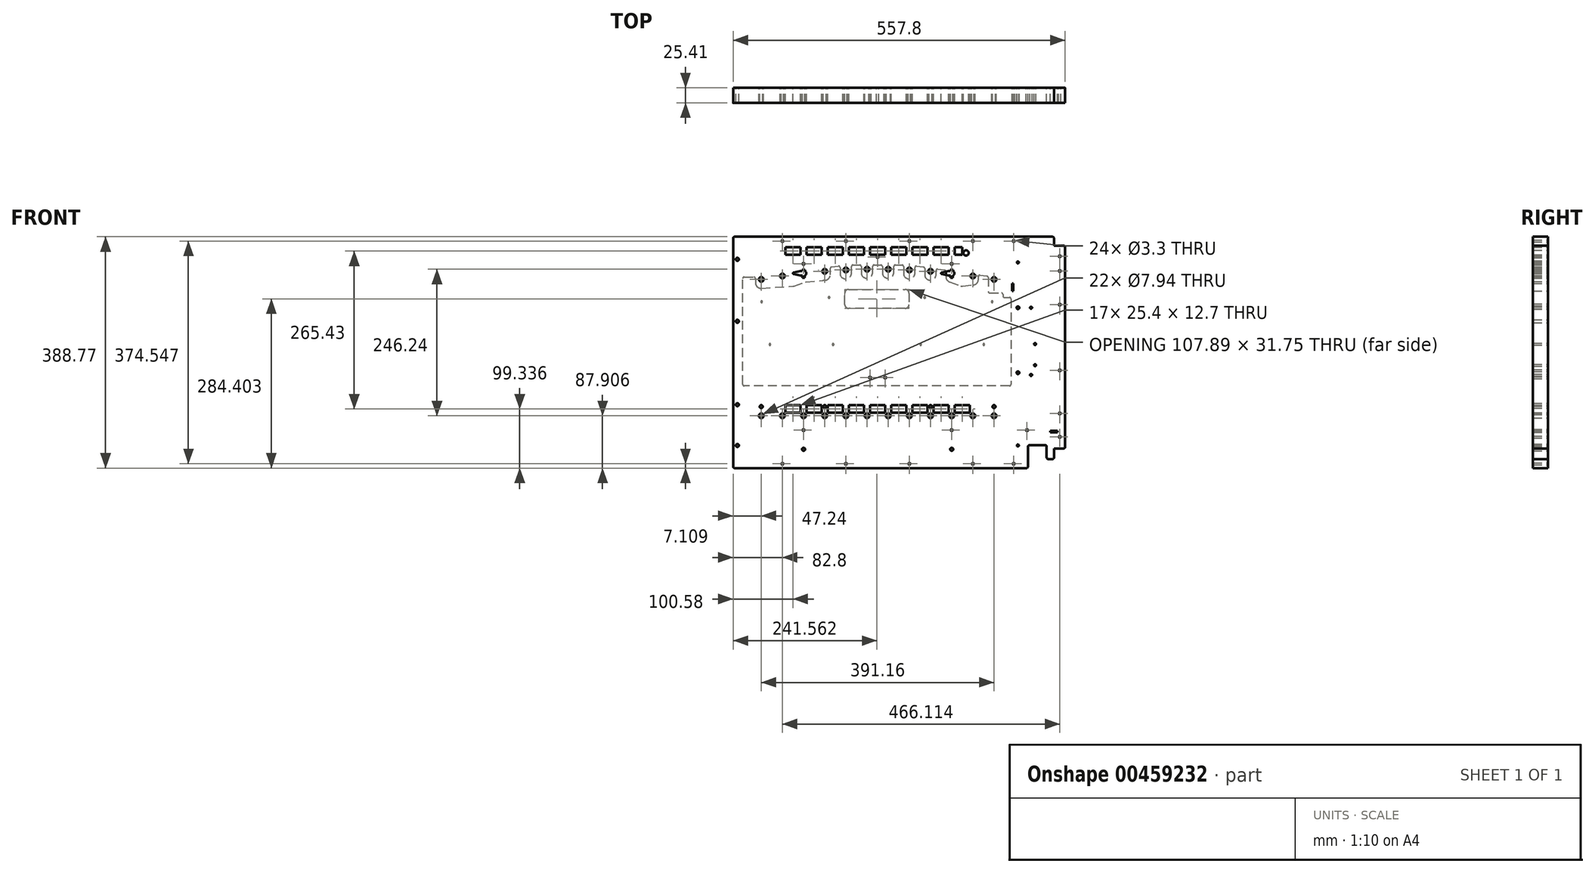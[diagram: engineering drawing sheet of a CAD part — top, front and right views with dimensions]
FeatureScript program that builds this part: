
annotation { "Feature Type Name" : "Feature", "Feature Type Description" : "" }
export const myFeature = defineFeature(function(context is Context, id is Id, definition is map)
    precondition{}
    {
        {
            var Q0;
            Q0=qCreatedBy(makeId("Front.planeOp"),FACE);
            var sketch = newSketch(context, id + "F0", { "sketchPlane" : qUnion([Q0])});
            skCircle(sketch, "E0", {"center": v(270.01, 168.97) * mm, "radius": 1.65 * mm});
            skCircle(sketch, "E1", {"center": v(270.01, 144.35) * mm, "radius": 1.65 * mm});
            skCircle(sketch, "E2", {"center": v(270.01, 87.69) * mm, "radius": 1.65 * mm});
            skCircle(sketch, "E3", {"center": v(270.01, -22.8) * mm, "radius": 1.65 * mm});
            skCircle(sketch, "E4", {"center": v(270.01, -134.56) * mm, "radius": 1.65 * mm});
            skCircle(sketch, "E5", {"center": v(270.01, -95.2) * mm, "radius": 1.65 * mm});
            skCircle(sketch, "E6", {"center": v(-196.1, -179.8) * mm, "radius": 1.65 * mm});
            skCircle(sketch, "E7", {"center": v(-89.42, -179.8) * mm, "radius": 1.65 * mm});
            skCircle(sketch, "E8", {"center": v(17.26, -179.8) * mm, "radius": 1.65 * mm});
            skCircle(sketch, "E9", {"center": v(123.94, -179.8) * mm, "radius": 1.65 * mm});
            skCircle(sketch, "E10", {"center": v(192.52, -179.8) * mm, "radius": 1.65 * mm});
            skCircle(sketch, "E11", {"center": v(-196.1, 194.75) * mm, "radius": 1.65 * mm});
            skCircle(sketch, "E12", {"center": v(-89.42, 194.75) * mm, "radius": 1.65 * mm});
            skCircle(sketch, "E13", {"center": v(17.26, 194.75) * mm, "radius": 1.65 * mm});
            skCircle(sketch, "E14", {"center": v(123.94, 194.75) * mm, "radius": 1.65 * mm});
            skCircle(sketch, "E15", {"center": v(192.52, 194.75) * mm, "radius": 1.65 * mm});
            skCircle(sketch, "E16", {"center": v(-196.1, 136) * mm, "radius": 3.97 * mm});
            skCircle(sketch, "E17", {"center": v(-124.98, 143.87) * mm, "radius": 3.97 * mm});
            skCircle(sketch, "E18", {"center": v(-89.42, 146.12) * mm, "radius": 3.97 * mm});
            skCircle(sketch, "E19", {"center": v(-53.86, 147.24) * mm, "radius": 3.97 * mm});
            skCircle(sketch, "E20", {"center": v(17.26, 146.12) * mm, "radius": 3.97 * mm});
            skCircle(sketch, "E21", {"center": v(-18.3, 147.24) * mm, "radius": 3.97 * mm});
            skCircle(sketch, "E22", {"center": v(52.82, 143.87) * mm, "radius": 3.97 * mm});
            skCircle(sketch, "E23", {"center": v(123.94, 136) * mm, "radius": 3.97 * mm});
            skCircle(sketch, "E24", {"center": v(-196.1, -99) * mm, "radius": 3.97 * mm});
            skCircle(sketch, "E25", {"center": v(-160.54, -99) * mm, "radius": 3.97 * mm});
            skCircle(sketch, "E26", {"center": v(-124.98, -99) * mm, "radius": 3.97 * mm});
            skCircle(sketch, "E27", {"center": v(-89.42, -99) * mm, "radius": 3.97 * mm});
            skCircle(sketch, "E28", {"center": v(-53.86, -99) * mm, "radius": 3.97 * mm});
            skCircle(sketch, "E29", {"center": v(-18.3, -99) * mm, "radius": 3.97 * mm});
            skCircle(sketch, "E30", {"center": v(17.26, -99) * mm, "radius": 3.97 * mm});
            skCircle(sketch, "E31", {"center": v(52.82, -99) * mm, "radius": 3.97 * mm});
            skCircle(sketch, "E32", {"center": v(88.38, -99) * mm, "radius": 3.97 * mm});
            skCircle(sketch, "E33", {"center": v(123.94, -99) * mm, "radius": 3.97 * mm});
            skCircle(sketch, "E34", {"center": v(159.5, 130.33) * mm, "radius": 3.97 * mm});
            skCircle(sketch, "E35", {"center": v(159.5, -99) * mm, "radius": 3.97 * mm});
            skCircle(sketch, "E36", {"center": v(-231.66, -99) * mm, "radius": 3.97 * mm});
            skCircle(sketch, "E37", {"center": v(-231.66, 130.33) * mm, "radius": 3.97 * mm});
            skCircle(sketch, "E38", {"center": v(-271.8, 163.89) * mm, "radius": 2.54 * mm});
            skCircle(sketch, "E39", {"center": v(-271.8, 59.75) * mm, "radius": 2.54 * mm});
            skCircle(sketch, "E40", {"center": v(-271.8, -148.94) * mm, "radius": 2.54 * mm});
            skCircle(sketch, "E41", {"center": v(-160.54, 156.27) * mm, "radius": 1.65 * mm});
            skCircle(sketch, "E42", {"center": v(88.38, 156.27) * mm, "radius": 1.65 * mm});
            skCircle(sketch, "E43", {"center": v(-36.08, 167.95) * mm, "radius": 1.65 * mm});
            skCircle(sketch, "E44", {"center": v(199.63, 82.6) * mm, "radius": 2.29 * mm});
            skCircle(sketch, "E45", {"center": v(221.73, 82.6) * mm, "radius": 1.66 * mm});
            skCircle(sketch, "E46", {"center": v(199.63, -26.61) * mm, "radius": 2.29 * mm});
            skCircle(sketch, "E47", {"center": v(221.73, -30.42) * mm, "radius": 1.66 * mm});
            skCircle(sketch, "E48", {"center": v(-160.54, -155.3) * mm, "radius": 2.54 * mm});
            skCircle(sketch, "E49", {"center": v(88.38, -155.3) * mm, "radius": 2.54 * mm});
            skCircle(sketch, "E50", {"center": v(-231.66, -83.76) * mm, "radius": 2.54 * mm});
            skCircle(sketch, "E51", {"center": v(159.5, -83.76) * mm, "radius": 2.54 * mm});
            skCircle(sketch, "E52", {"center": v(-160.54, -123.13) * mm, "radius": 1.65 * mm});
            skCircle(sketch, "E53", {"center": v(88.38, -123.13) * mm, "radius": 1.65 * mm});
            skCircle(sketch, "E54", {"center": v(-271.8, -80.36) * mm, "radius": 2.54 * mm});
            skCircle(sketch, "E55", {"center": v(-124.98, -83.76) * mm, "radius": 2.54 * mm});
            skCircle(sketch, "E56", {"center": v(52.82, -83.76) * mm, "radius": 2.54 * mm});
            skCircle(sketch, "E57", {"center": v(228.49, -13.91) * mm, "radius": 1.66 * mm});
            skCircle(sketch, "E58", {"center": v(228.49, 21.65) * mm, "radius": 1.66 * mm});
            skCircle(sketch, "E59", {"center": v(112.5, 174.6) * mm, "radius": 4.45 * mm});
            skCircle(sketch, "E60", {"center": v(199.63, 158.8) * mm, "radius": 1.66 * mm});
            skCircle(sketch, "E61", {"center": v(199.63, -148.94) * mm, "radius": 1.66 * mm});
            skCircle(sketch, "E62", {"center": v(-48.78, -34.87) * mm, "radius": 1.65 * mm});
            skCircle(sketch, "E63", {"center": v(-23.38, -34.87) * mm, "radius": 1.65 * mm});
            skCircle(sketch, "E64", {"center": v(214.97, -123.13) * mm, "radius": 1.65 * mm});
            skLineSegment(sketch, "E65", {"start": v(-48.78, 171.5) * mm, "end": v(-23.38, 171.5) * mm});
            skLineSegment(sketch, "E66", {"start": v(-23.38, 171.5) * mm, "end": v(-23.38, 184.2) * mm});
            skLineSegment(sketch, "E67", {"start": v(-23.38, 184.2) * mm, "end": v(-48.78, 184.2) * mm});
            skLineSegment(sketch, "E68", {"start": v(-48.78, 184.2) * mm, "end": v(-48.78, 171.5) * mm});
            skLineSegment(sketch, "E69", {"start": v(-58.94, 184.2) * mm, "end": v(-84.34, 184.2) * mm});
            skLineSegment(sketch, "E70", {"start": v(-84.34, 184.2) * mm, "end": v(-84.34, 171.5) * mm});
            skLineSegment(sketch, "E71", {"start": v(-84.34, 171.5) * mm, "end": v(-58.94, 171.5) * mm});
            skLineSegment(sketch, "E72", {"start": v(-58.94, 171.5) * mm, "end": v(-58.94, 184.2) * mm});
            skLineSegment(sketch, "E73", {"start": v(-94.5, 184.2) * mm, "end": v(-119.9, 184.2) * mm});
            skLineSegment(sketch, "E74", {"start": v(-119.9, 184.2) * mm, "end": v(-119.9, 171.5) * mm});
            skLineSegment(sketch, "E75", {"start": v(-119.9, 171.5) * mm, "end": v(-94.5, 171.5) * mm});
            skLineSegment(sketch, "E76", {"start": v(-94.5, 171.5) * mm, "end": v(-94.5, 184.2) * mm});
            skLineSegment(sketch, "E77", {"start": v(-130.06, 184.2) * mm, "end": v(-155.46, 184.2) * mm});
            skLineSegment(sketch, "E78", {"start": v(-155.46, 184.2) * mm, "end": v(-155.46, 171.5) * mm});
            skLineSegment(sketch, "E79", {"start": v(-155.46, 171.5) * mm, "end": v(-130.06, 171.5) * mm});
            skLineSegment(sketch, "E80", {"start": v(-130.06, 171.5) * mm, "end": v(-130.06, 184.2) * mm});
            skLineSegment(sketch, "E81", {"start": v(-165.62, 184.2) * mm, "end": v(-191.02, 184.2) * mm});
            skLineSegment(sketch, "E82", {"start": v(-191.02, 184.2) * mm, "end": v(-191.02, 171.5) * mm});
            skLineSegment(sketch, "E83", {"start": v(-191.02, 171.5) * mm, "end": v(-165.62, 171.5) * mm});
            skLineSegment(sketch, "E84", {"start": v(-165.62, 171.5) * mm, "end": v(-165.62, 184.2) * mm});
            skLineSegment(sketch, "E85", {"start": v(-13.22, 171.5) * mm, "end": v(12.18, 171.5) * mm});
            skLineSegment(sketch, "E86", {"start": v(12.18, 171.5) * mm, "end": v(12.18, 184.2) * mm});
            skLineSegment(sketch, "E87", {"start": v(12.18, 184.2) * mm, "end": v(-13.22, 184.2) * mm});
            skLineSegment(sketch, "E88", {"start": v(-13.22, 184.2) * mm, "end": v(-13.22, 171.5) * mm});
            skLineSegment(sketch, "E89", {"start": v(22.34, 171.5) * mm, "end": v(47.74, 171.5) * mm});
            skLineSegment(sketch, "E90", {"start": v(47.74, 171.5) * mm, "end": v(47.74, 184.2) * mm});
            skLineSegment(sketch, "E91", {"start": v(47.74, 184.2) * mm, "end": v(22.34, 184.2) * mm});
            skLineSegment(sketch, "E92", {"start": v(22.34, 184.2) * mm, "end": v(22.34, 171.5) * mm});
            skLineSegment(sketch, "E93", {"start": v(57.9, 171.5) * mm, "end": v(83.3, 171.5) * mm});
            skLineSegment(sketch, "E94", {"start": v(83.3, 171.5) * mm, "end": v(83.3, 184.2) * mm});
            skLineSegment(sketch, "E95", {"start": v(83.3, 184.2) * mm, "end": v(57.9, 184.2) * mm});
            skLineSegment(sketch, "E96", {"start": v(57.9, 184.2) * mm, "end": v(57.9, 171.5) * mm});
            skLineSegment(sketch, "E97", {"start": v(93.46, 171.5) * mm, "end": v(106.16, 171.5) * mm});
            skLineSegment(sketch, "E98", {"start": v(106.16, 171.5) * mm, "end": v(106.16, 184.2) * mm});
            skLineSegment(sketch, "E99", {"start": v(106.16, 184.2) * mm, "end": v(93.46, 184.2) * mm});
            skLineSegment(sketch, "E100", {"start": v(93.46, 184.2) * mm, "end": v(93.46, 171.5) * mm});
            skLineSegment(sketch, "E101", {"start": v(-48.78, -93.92) * mm, "end": v(-23.38, -93.92) * mm});
            skLineSegment(sketch, "E102", {"start": v(-23.38, -93.92) * mm, "end": v(-23.38, -81.22) * mm});
            skLineSegment(sketch, "E103", {"start": v(-23.38, -81.22) * mm, "end": v(-48.78, -81.22) * mm});
            skLineSegment(sketch, "E104", {"start": v(-48.78, -81.22) * mm, "end": v(-48.78, -93.92) * mm});
            skLineSegment(sketch, "E105", {"start": v(-58.94, -81.22) * mm, "end": v(-84.34, -81.22) * mm});
            skLineSegment(sketch, "E106", {"start": v(-84.34, -81.22) * mm, "end": v(-84.34, -93.92) * mm});
            skLineSegment(sketch, "E107", {"start": v(-84.34, -93.92) * mm, "end": v(-58.94, -93.92) * mm});
            skLineSegment(sketch, "E108", {"start": v(-58.94, -93.92) * mm, "end": v(-58.94, -81.22) * mm});
            skLineSegment(sketch, "E109", {"start": v(-94.5, -81.22) * mm, "end": v(-119.9, -81.22) * mm});
            skLineSegment(sketch, "E110", {"start": v(-119.9, -81.22) * mm, "end": v(-119.9, -93.92) * mm});
            skLineSegment(sketch, "E111", {"start": v(-119.9, -93.92) * mm, "end": v(-94.5, -93.92) * mm});
            skLineSegment(sketch, "E112", {"start": v(-94.5, -93.92) * mm, "end": v(-94.5, -81.22) * mm});
            skLineSegment(sketch, "E113", {"start": v(-130.06, -81.22) * mm, "end": v(-155.46, -81.22) * mm});
            skLineSegment(sketch, "E114", {"start": v(-155.46, -81.22) * mm, "end": v(-155.46, -93.92) * mm});
            skLineSegment(sketch, "E115", {"start": v(-155.46, -93.92) * mm, "end": v(-130.06, -93.92) * mm});
            skLineSegment(sketch, "E116", {"start": v(-130.06, -93.92) * mm, "end": v(-130.06, -81.22) * mm});
            skLineSegment(sketch, "E117", {"start": v(-165.62, -81.22) * mm, "end": v(-191.02, -81.22) * mm});
            skLineSegment(sketch, "E118", {"start": v(-191.02, -81.22) * mm, "end": v(-191.02, -93.92) * mm});
            skLineSegment(sketch, "E119", {"start": v(-191.02, -93.92) * mm, "end": v(-165.62, -93.92) * mm});
            skLineSegment(sketch, "E120", {"start": v(-165.62, -93.92) * mm, "end": v(-165.62, -81.22) * mm});
            skLineSegment(sketch, "E121", {"start": v(-13.22, -93.92) * mm, "end": v(12.18, -93.92) * mm});
            skLineSegment(sketch, "E122", {"start": v(12.18, -93.92) * mm, "end": v(12.18, -81.22) * mm});
            skLineSegment(sketch, "E123", {"start": v(12.18, -81.22) * mm, "end": v(-13.22, -81.22) * mm});
            skLineSegment(sketch, "E124", {"start": v(-13.22, -81.22) * mm, "end": v(-13.22, -93.92) * mm});
            skLineSegment(sketch, "E125", {"start": v(22.34, -93.92) * mm, "end": v(47.74, -93.92) * mm});
            skLineSegment(sketch, "E126", {"start": v(47.74, -93.92) * mm, "end": v(47.74, -81.22) * mm});
            skLineSegment(sketch, "E127", {"start": v(47.74, -81.22) * mm, "end": v(22.34, -81.22) * mm});
            skLineSegment(sketch, "E128", {"start": v(22.34, -81.22) * mm, "end": v(22.34, -93.92) * mm});
            skLineSegment(sketch, "E129", {"start": v(57.9, -93.92) * mm, "end": v(83.3, -93.92) * mm});
            skLineSegment(sketch, "E130", {"start": v(83.3, -93.92) * mm, "end": v(83.3, -81.22) * mm});
            skLineSegment(sketch, "E131", {"start": v(83.3, -81.22) * mm, "end": v(57.9, -81.22) * mm});
            skLineSegment(sketch, "E132", {"start": v(57.9, -81.22) * mm, "end": v(57.9, -93.92) * mm});
            skLineSegment(sketch, "E133", {"start": v(93.46, -93.92) * mm, "end": v(118.86, -93.92) * mm});
            skLineSegment(sketch, "E134", {"start": v(118.86, -93.92) * mm, "end": v(118.86, -81.22) * mm});
            skLineSegment(sketch, "E135", {"start": v(118.86, -81.22) * mm, "end": v(93.46, -81.22) * mm});
            skLineSegment(sketch, "E136", {"start": v(93.46, -81.22) * mm, "end": v(93.46, -93.92) * mm});
            skLineSegment(sketch, "E137", {"start": v(-163.33, 145.92) * mm, "end": v(-163.33, 144.06) * mm});
            skLineSegment(sketch, "E138", {"start": v(-163.33, 144.06) * mm, "end": v(-165.62, 144.06) * mm});
            skLineSegment(sketch, "E139", {"start": v(-165.62, 144.06) * mm, "end": v(-177.3, 141.75) * mm});
            skLineSegment(sketch, "E140", {"start": v(-177.3, 139.26) * mm, "end": v(-165.62, 136.95) * mm});
            skLineSegment(sketch, "E141", {"start": v(-165.62, 136.95) * mm, "end": v(-163.2, 136.95) * mm});
            skLineSegment(sketch, "E142", {"start": v(-162.32, 136.43) * mm, "end": v(-162.32, 133.1) * mm});
            skLineSegment(sketch, "E143", {"start": v(-158.76, 133.1) * mm, "end": v(-158.76, 136.43) * mm});
            skLineSegment(sketch, "E144", {"start": v(-157.75, 143.96) * mm, "end": v(-157.75, 145.92) * mm});
            skLineSegment(sketch, "E145", {"start": v(85.59, 145.92) * mm, "end": v(85.59, 144.06) * mm});
            skLineSegment(sketch, "E146", {"start": v(85.59, 144.06) * mm, "end": v(83.3, 144.06) * mm});
            skLineSegment(sketch, "E147", {"start": v(83.3, 144.06) * mm, "end": v(71.62, 141.75) * mm});
            skLineSegment(sketch, "E148", {"start": v(71.62, 139.26) * mm, "end": v(83.3, 136.95) * mm});
            skLineSegment(sketch, "E149", {"start": v(83.3, 136.95) * mm, "end": v(85.71, 136.95) * mm});
            skLineSegment(sketch, "E150", {"start": v(86.6, 136.43) * mm, "end": v(86.6, 133.1) * mm});
            skLineSegment(sketch, "E151", {"start": v(90.16, 133.1) * mm, "end": v(90.16, 136.43) * mm});
            skLineSegment(sketch, "E152", {"start": v(91.17, 143.96) * mm, "end": v(91.17, 145.92) * mm});
            skLineSegment(sketch, "E153", {"start": v(189.95, 110.55) * mm, "end": v(191.63, 110.55) * mm});
            skLineSegment(sketch, "E154", {"start": v(191.63, 110.55) * mm, "end": v(191.63, 123.25) * mm});
            skLineSegment(sketch, "E155", {"start": v(191.63, 123.25) * mm, "end": v(189.95, 123.25) * mm});
            skLineSegment(sketch, "E156", {"start": v(189.95, 123.25) * mm, "end": v(189.95, 110.55) * mm});
            skLineSegment(sketch, "E157", {"start": v(253.89, -124.4) * mm, "end": v(253.89, -126.94) * mm});
            skLineSegment(sketch, "E158", {"start": v(253.89, -126.94) * mm, "end": v(266.2, -126.94) * mm});
            skLineSegment(sketch, "E159", {"start": v(266.2, -126.94) * mm, "end": v(266.2, -124.4) * mm});
            skLineSegment(sketch, "E160", {"start": v(266.2, -124.4) * mm, "end": v(253.89, -124.4) * mm});
            skLineSegment(sketch, "E161", {"start": v(278.9, -151.48) * mm, "end": v(278.9, 184.2) * mm});
            skLineSegment(sketch, "E162", {"start": v(260.24, -154.02) * mm, "end": v(276.36, -154.02) * mm});
            skLineSegment(sketch, "E163", {"start": v(260.24, -169.26) * mm, "end": v(260.24, -154.02) * mm});
            skLineSegment(sketch, "E164", {"start": v(250.58, -171.8) * mm, "end": v(257.7, -171.8) * mm});
            skLineSegment(sketch, "E165", {"start": v(248.04, -150.97) * mm, "end": v(248.04, -169.26) * mm});
            skLineSegment(sketch, "E166", {"start": v(219.09, -148.43) * mm, "end": v(245.5, -148.43) * mm});
            skLineSegment(sketch, "E167", {"start": v(216.55, -184.37) * mm, "end": v(216.55, -150.97) * mm});
            skLineSegment(sketch, "E168", {"start": v(-276.36, -186.91) * mm, "end": v(214, -186.91) * mm});
            skLineSegment(sketch, "E169", {"start": v(-278.9, 199.32) * mm, "end": v(-278.9, -184.37) * mm});
            skLineSegment(sketch, "E170", {"start": v(257.7, 201.86) * mm, "end": v(-276.36, 201.86) * mm});
            skLineSegment(sketch, "E171", {"start": v(260.24, 186.75) * mm, "end": v(260.24, 199.32) * mm});
            skLineSegment(sketch, "E172", {"start": v(276.36, 186.75) * mm, "end": v(260.24, 186.75) * mm});
            skArc(sketch, "E173", {"start": v(-177.3, 141.75) * mm, "mid": v(-178.32, 140.5) * mm, "end": v(-177.3, 139.26) * mm});
            skArc(sketch, "E174", {"start": v(-163.2, 136.95) * mm, "mid": v(-162.78, 136.66) * mm, "end": v(-162.32, 136.43) * mm});
            skArc(sketch, "E175", {"start": v(-162.32, 133.1) * mm, "mid": v(-160.54, 132.88) * mm, "end": v(-158.76, 133.1) * mm});
            skArc(sketch, "E176", {"start": v(-158.76, 136.43) * mm, "mid": v(-156.14, 139.9) * mm, "end": v(-157.75, 143.96) * mm});
            skArc(sketch, "E177", {"start": v(-157.75, 145.92) * mm, "mid": v(-160.54, 146.6) * mm, "end": v(-163.33, 145.92) * mm});
            skArc(sketch, "E178", {"start": v(71.62, 141.75) * mm, "mid": v(70.6, 140.5) * mm, "end": v(71.62, 139.26) * mm});
            skArc(sketch, "E179", {"start": v(85.71, 136.95) * mm, "mid": v(86.14, 136.66) * mm, "end": v(86.6, 136.43) * mm});
            skArc(sketch, "E180", {"start": v(86.6, 133.1) * mm, "mid": v(88.38, 132.88) * mm, "end": v(90.16, 133.1) * mm});
            skArc(sketch, "E181", {"start": v(90.16, 136.43) * mm, "mid": v(92.78, 139.9) * mm, "end": v(91.17, 143.96) * mm});
            skArc(sketch, "E182", {"start": v(91.17, 145.92) * mm, "mid": v(88.38, 146.6) * mm, "end": v(85.59, 145.92) * mm});
            skArc(sketch, "E183", {"start": v(276.36, -154.02) * mm, "mid": v(278.16, -153.28) * mm, "end": v(278.9, -151.48) * mm});
            skArc(sketch, "E184", {"start": v(257.7, -171.8) * mm, "mid": v(259.5, -171.06) * mm, "end": v(260.24, -169.26) * mm});
            skArc(sketch, "E185", {"start": v(248.04, -169.26) * mm, "mid": v(248.79, -171.06) * mm, "end": v(250.58, -171.8) * mm});
            skArc(sketch, "E186", {"start": v(248.04, -150.97) * mm, "mid": v(247.3, -149.18) * mm, "end": v(245.5, -148.43) * mm});
            skArc(sketch, "E187", {"start": v(219.09, -148.43) * mm, "mid": v(217.3, -149.18) * mm, "end": v(216.55, -150.97) * mm});
            skArc(sketch, "E188", {"start": v(214, -186.91) * mm, "mid": v(215.8, -186.17) * mm, "end": v(216.55, -184.37) * mm});
            skArc(sketch, "E189", {"start": v(-278.9, -184.37) * mm, "mid": v(-278.16, -186.17) * mm, "end": v(-276.36, -186.91) * mm});
            skArc(sketch, "E190", {"start": v(-276.36, 201.86) * mm, "mid": v(-278.16, 201.11) * mm, "end": v(-278.9, 199.32) * mm});
            skArc(sketch, "E191", {"start": v(260.24, 199.32) * mm, "mid": v(259.5, 201.11) * mm, "end": v(257.7, 201.86) * mm});
            skArc(sketch, "E192", {"start": v(278.9, 184.2) * mm, "mid": v(278.16, 186) * mm, "end": v(276.36, 186.75) * mm});
            skSolve(sketch);
        }
        {
            var Q0;
            Q0=qSketchRegion(id+"F0",true);
            extrude(context, id + "F1", {"entities" : qUnion([Q0]), "depth" : 25.4 * mm});
        }
        {
            var Q0;
            Q0=makeQuery(id+"F1.opExtrude","CAP_FACE",FACE,{"disambiguationData":[OSD([sQuery(id+"F0.wireOp",EDGE,"E0"),sQuery(id+"F0.wireOp",EDGE,"E1"),sQuery(id+"F0.wireOp",EDGE,"E2"),sQuery(id+"F0.wireOp",EDGE,"E3"),sQuery(id+"F0.wireOp",EDGE,"E4"),sQuery(id+"F0.wireOp",EDGE,"E5"),sQuery(id+"F0.wireOp",EDGE,"E6"),sQuery(id+"F0.wireOp",EDGE,"E7"),sQuery(id+"F0.wireOp",EDGE,"E8"),sQuery(id+"F0.wireOp",EDGE,"E9"),sQuery(id+"F0.wireOp",EDGE,"E10"),sQuery(id+"F0.wireOp",EDGE,"E11"),sQuery(id+"F0.wireOp",EDGE,"E12"),sQuery(id+"F0.wireOp",EDGE,"E13"),sQuery(id+"F0.wireOp",EDGE,"E14"),sQuery(id+"F0.wireOp",EDGE,"E15"),sQuery(id+"F0.wireOp",EDGE,"E16"),sQuery(id+"F0.wireOp",EDGE,"E17"),sQuery(id+"F0.wireOp",EDGE,"E18"),sQuery(id+"F0.wireOp",EDGE,"E19"),sQuery(id+"F0.wireOp",EDGE,"E20"),sQuery(id+"F0.wireOp",EDGE,"E21"),sQuery(id+"F0.wireOp",EDGE,"E22"),sQuery(id+"F0.wireOp",EDGE,"E23"),sQuery(id+"F0.wireOp",EDGE,"E24"),sQuery(id+"F0.wireOp",EDGE,"E25"),sQuery(id+"F0.wireOp",EDGE,"E26"),sQuery(id+"F0.wireOp",EDGE,"E27"),sQuery(id+"F0.wireOp",EDGE,"E28"),sQuery(id+"F0.wireOp",EDGE,"E29"),sQuery(id+"F0.wireOp",EDGE,"E30"),sQuery(id+"F0.wireOp",EDGE,"E31"),sQuery(id+"F0.wireOp",EDGE,"E32"),sQuery(id+"F0.wireOp",EDGE,"E33"),sQuery(id+"F0.wireOp",EDGE,"E34"),sQuery(id+"F0.wireOp",EDGE,"E35"),sQuery(id+"F0.wireOp",EDGE,"E36"),sQuery(id+"F0.wireOp",EDGE,"E37"),sQuery(id+"F0.wireOp",EDGE,"E38"),sQuery(id+"F0.wireOp",EDGE,"E39"),sQuery(id+"F0.wireOp",EDGE,"E40"),sQuery(id+"F0.wireOp",EDGE,"E41"),sQuery(id+"F0.wireOp",EDGE,"E42"),sQuery(id+"F0.wireOp",EDGE,"E43"),sQuery(id+"F0.wireOp",EDGE,"E44"),sQuery(id+"F0.wireOp",EDGE,"E45"),sQuery(id+"F0.wireOp",EDGE,"E46"),sQuery(id+"F0.wireOp",EDGE,"E47"),sQuery(id+"F0.wireOp",EDGE,"E48"),sQuery(id+"F0.wireOp",EDGE,"E49"),sQuery(id+"F0.wireOp",EDGE,"E50"),sQuery(id+"F0.wireOp",EDGE,"E51"),sQuery(id+"F0.wireOp",EDGE,"E52"),sQuery(id+"F0.wireOp",EDGE,"E53"),sQuery(id+"F0.wireOp",EDGE,"E54"),sQuery(id+"F0.wireOp",EDGE,"E55"),sQuery(id+"F0.wireOp",EDGE,"E56"),sQuery(id+"F0.wireOp",EDGE,"E57"),sQuery(id+"F0.wireOp",EDGE,"E58"),sQuery(id+"F0.wireOp",EDGE,"E59"),sQuery(id+"F0.wireOp",EDGE,"E60"),sQuery(id+"F0.wireOp",EDGE,"E61"),sQuery(id+"F0.wireOp",EDGE,"E62"),sQuery(id+"F0.wireOp",EDGE,"E63"),sQuery(id+"F0.wireOp",EDGE,"E64"),sQuery(id+"F0.wireOp",EDGE,"E65"),sQuery(id+"F0.wireOp",EDGE,"E66"),sQuery(id+"F0.wireOp",EDGE,"E67"),sQuery(id+"F0.wireOp",EDGE,"E68"),sQuery(id+"F0.wireOp",EDGE,"E69"),sQuery(id+"F0.wireOp",EDGE,"E70"),sQuery(id+"F0.wireOp",EDGE,"E71"),sQuery(id+"F0.wireOp",EDGE,"E72"),sQuery(id+"F0.wireOp",EDGE,"E73"),sQuery(id+"F0.wireOp",EDGE,"E74"),sQuery(id+"F0.wireOp",EDGE,"E75"),sQuery(id+"F0.wireOp",EDGE,"E76"),sQuery(id+"F0.wireOp",EDGE,"E77"),sQuery(id+"F0.wireOp",EDGE,"E78"),sQuery(id+"F0.wireOp",EDGE,"E79"),sQuery(id+"F0.wireOp",EDGE,"E80"),sQuery(id+"F0.wireOp",EDGE,"E81"),sQuery(id+"F0.wireOp",EDGE,"E82"),sQuery(id+"F0.wireOp",EDGE,"E83"),sQuery(id+"F0.wireOp",EDGE,"E84"),sQuery(id+"F0.wireOp",EDGE,"E85"),sQuery(id+"F0.wireOp",EDGE,"E86"),sQuery(id+"F0.wireOp",EDGE,"E87"),sQuery(id+"F0.wireOp",EDGE,"E88"),sQuery(id+"F0.wireOp",EDGE,"E89"),sQuery(id+"F0.wireOp",EDGE,"E90"),sQuery(id+"F0.wireOp",EDGE,"E91"),sQuery(id+"F0.wireOp",EDGE,"E92"),sQuery(id+"F0.wireOp",EDGE,"E93"),sQuery(id+"F0.wireOp",EDGE,"E94"),sQuery(id+"F0.wireOp",EDGE,"E95"),sQuery(id+"F0.wireOp",EDGE,"E96"),sQuery(id+"F0.wireOp",EDGE,"E97"),sQuery(id+"F0.wireOp",EDGE,"E98"),sQuery(id+"F0.wireOp",EDGE,"E99"),sQuery(id+"F0.wireOp",EDGE,"E100"),sQuery(id+"F0.wireOp",EDGE,"E101"),sQuery(id+"F0.wireOp",EDGE,"E102"),sQuery(id+"F0.wireOp",EDGE,"E103"),sQuery(id+"F0.wireOp",EDGE,"E104"),sQuery(id+"F0.wireOp",EDGE,"E105"),sQuery(id+"F0.wireOp",EDGE,"E106"),sQuery(id+"F0.wireOp",EDGE,"E107"),sQuery(id+"F0.wireOp",EDGE,"E108"),sQuery(id+"F0.wireOp",EDGE,"E109"),sQuery(id+"F0.wireOp",EDGE,"E110"),sQuery(id+"F0.wireOp",EDGE,"E111"),sQuery(id+"F0.wireOp",EDGE,"E112"),sQuery(id+"F0.wireOp",EDGE,"E113"),sQuery(id+"F0.wireOp",EDGE,"E114"),sQuery(id+"F0.wireOp",EDGE,"E115"),sQuery(id+"F0.wireOp",EDGE,"E116"),sQuery(id+"F0.wireOp",EDGE,"E117"),sQuery(id+"F0.wireOp",EDGE,"E118"),sQuery(id+"F0.wireOp",EDGE,"E119"),sQuery(id+"F0.wireOp",EDGE,"E120"),sQuery(id+"F0.wireOp",EDGE,"E121"),sQuery(id+"F0.wireOp",EDGE,"E122"),sQuery(id+"F0.wireOp",EDGE,"E123"),sQuery(id+"F0.wireOp",EDGE,"E124"),sQuery(id+"F0.wireOp",EDGE,"E125"),sQuery(id+"F0.wireOp",EDGE,"E126"),sQuery(id+"F0.wireOp",EDGE,"E127"),sQuery(id+"F0.wireOp",EDGE,"E128"),sQuery(id+"F0.wireOp",EDGE,"E129"),sQuery(id+"F0.wireOp",EDGE,"E130"),sQuery(id+"F0.wireOp",EDGE,"E131"),sQuery(id+"F0.wireOp",EDGE,"E132"),sQuery(id+"F0.wireOp",EDGE,"E133"),sQuery(id+"F0.wireOp",EDGE,"E134"),sQuery(id+"F0.wireOp",EDGE,"E135"),sQuery(id+"F0.wireOp",EDGE,"E136"),sQuery(id+"F0.wireOp",EDGE,"E137"),sQuery(id+"F0.wireOp",EDGE,"E138"),sQuery(id+"F0.wireOp",EDGE,"E139"),sQuery(id+"F0.wireOp",EDGE,"E140"),sQuery(id+"F0.wireOp",EDGE,"E141"),sQuery(id+"F0.wireOp",EDGE,"E142"),sQuery(id+"F0.wireOp",EDGE,"E143"),sQuery(id+"F0.wireOp",EDGE,"E144"),sQuery(id+"F0.wireOp",EDGE,"E145"),sQuery(id+"F0.wireOp",EDGE,"E146"),sQuery(id+"F0.wireOp",EDGE,"E147"),sQuery(id+"F0.wireOp",EDGE,"E148"),sQuery(id+"F0.wireOp",EDGE,"E149"),sQuery(id+"F0.wireOp",EDGE,"E150"),sQuery(id+"F0.wireOp",EDGE,"E151"),sQuery(id+"F0.wireOp",EDGE,"E152"),sQuery(id+"F0.wireOp",EDGE,"E153"),sQuery(id+"F0.wireOp",EDGE,"E154"),sQuery(id+"F0.wireOp",EDGE,"E155"),sQuery(id+"F0.wireOp",EDGE,"E156"),sQuery(id+"F0.wireOp",EDGE,"E157"),sQuery(id+"F0.wireOp",EDGE,"E158"),sQuery(id+"F0.wireOp",EDGE,"E159"),sQuery(id+"F0.wireOp",EDGE,"E160"),sQuery(id+"F0.wireOp",EDGE,"E161"),sQuery(id+"F0.wireOp",EDGE,"E162"),sQuery(id+"F0.wireOp",EDGE,"E163"),sQuery(id+"F0.wireOp",EDGE,"E164"),sQuery(id+"F0.wireOp",EDGE,"E165"),sQuery(id+"F0.wireOp",EDGE,"E166"),sQuery(id+"F0.wireOp",EDGE,"E167"),sQuery(id+"F0.wireOp",EDGE,"E168"),sQuery(id+"F0.wireOp",EDGE,"E169"),sQuery(id+"F0.wireOp",EDGE,"E170"),sQuery(id+"F0.wireOp",EDGE,"E171"),sQuery(id+"F0.wireOp",EDGE,"E172"),sQuery(id+"F0.wireOp",EDGE,"E173"),sQuery(id+"F0.wireOp",EDGE,"E174"),sQuery(id+"F0.wireOp",EDGE,"E175"),sQuery(id+"F0.wireOp",EDGE,"E176"),sQuery(id+"F0.wireOp",EDGE,"E177"),sQuery(id+"F0.wireOp",EDGE,"E178"),sQuery(id+"F0.wireOp",EDGE,"E179"),sQuery(id+"F0.wireOp",EDGE,"E180"),sQuery(id+"F0.wireOp",EDGE,"E181"),sQuery(id+"F0.wireOp",EDGE,"E182"),sQuery(id+"F0.wireOp",EDGE,"E183"),sQuery(id+"F0.wireOp",EDGE,"E184"),sQuery(id+"F0.wireOp",EDGE,"E185"),sQuery(id+"F0.wireOp",EDGE,"E186"),sQuery(id+"F0.wireOp",EDGE,"E187"),sQuery(id+"F0.wireOp",EDGE,"E188"),sQuery(id+"F0.wireOp",EDGE,"E189"),sQuery(id+"F0.wireOp",EDGE,"E190"),sQuery(id+"F0.wireOp",EDGE,"E191"),sQuery(id+"F0.wireOp",EDGE,"E192")])],"isStart":true});
            var sketch = newSketch(context, id + "F2", { "sketchPlane" : qUnion([Q0])});
            skCircle(sketch, "E193", {"center": v(179.69, -32.1) * mm, "radius": 1.46 * mm});
            skCircle(sketch, "E194", {"center": v(80.4, 47) * mm, "radius": 1.46 * mm});
            skCircle(sketch, "E195", {"center": v(-80.4, 47) * mm, "radius": 1.46 * mm});
            skCircle(sketch, "E196", {"center": v(-179.69, -32.1) * mm, "radius": 1.46 * mm});
            skLineSegment(sketch, "E197", {"start": v(-225.43, 44.45) * mm, "end": v(-225.43, -99.06) * mm});
            skArc(sketch, "E198", {"start": v(-225.43, -99.06) * mm, "mid": v(-224.68, -100.86) * mm, "end": v(-222.89, -101.6) * mm});
            skLineSegment(sketch, "E199", {"start": v(-222.89, -101.6) * mm, "end": v(222.88, -101.6) * mm});
            skArc(sketch, "E200", {"start": v(222.88, -101.6) * mm, "mid": v(224.68, -100.86) * mm, "end": v(225.42, -99.06) * mm});
            skLineSegment(sketch, "E201", {"start": v(225.43, -99.06) * mm, "end": v(225.43, 78.74) * mm});
            skArc(sketch, "E202", {"start": v(225.42, 78.74) * mm, "mid": v(224.68, 80.54) * mm, "end": v(222.88, 81.28) * mm});
            skLineSegment(sketch, "E203", {"start": v(222.88, 81.28) * mm, "end": v(206.63, 81.28) * mm});
            skArc(sketch, "E204", {"start": v(206.63, 81.28) * mm, "mid": v(204.83, 80.54) * mm, "end": v(204.09, 78.74) * mm});
            skLineSegment(sketch, "E205", {"start": v(204.09, 78.74) * mm, "end": v(204.09, 71.85) * mm});
            skArc(sketch, "E206", {"start": v(193.92, 62.35) * mm, "mid": v(201.07, 64.9) * mm, "end": v(204.09, 71.85) * mm});
            skLineSegment(sketch, "E207", {"start": v(193.92, 62.35) * mm, "end": v(140.8, 65.96) * mm});
            skArc(sketch, "E208", {"start": v(139.09, 66.32) * mm, "mid": v(139.93, 66.08) * mm, "end": v(140.8, 65.96) * mm});
            skLineSegment(sketch, "E209", {"start": v(139.09, 66.32) * mm, "end": v(120.24, 73.06) * mm});
            skArc(sketch, "E210", {"start": v(113.92, 82.03) * mm, "mid": v(115.66, 76.54) * mm, "end": v(120.24, 73.06) * mm});
            skLineSegment(sketch, "E211", {"start": v(113.92, 82.03) * mm, "end": v(113.92, 90.6) * mm});
            skArc(sketch, "E212", {"start": v(113.92, 90.6) * mm, "mid": v(113.3, 92.26) * mm, "end": v(111.74, 93.1) * mm});
            skLineSegment(sketch, "E213", {"start": v(111.74, 93.1) * mm, "end": v(100.3, 94.74) * mm});
            skArc(sketch, "E214", {"start": v(100.3, 94.74) * mm, "mid": v(98.28, 94.15) * mm, "end": v(97.4, 92.23) * mm});
            skLineSegment(sketch, "E215", {"start": v(97.4, 92.23) * mm, "end": v(97.4, 85.4) * mm});
            skArc(sketch, "E216", {"start": v(78.36, 85.4) * mm, "mid": v(87.88, 75.87) * mm, "end": v(97.4, 85.4) * mm});
            skLineSegment(sketch, "E217", {"start": v(78.36, 85.4) * mm, "end": v(78.36, 95.67) * mm});
            skArc(sketch, "E218", {"start": v(78.36, 95.67) * mm, "mid": v(77.74, 97.34) * mm, "end": v(76.18, 98.19) * mm});
            skLineSegment(sketch, "E219", {"start": v(76.18, 98.19) * mm, "end": v(64.75, 99.82) * mm});
            skArc(sketch, "E220", {"start": v(64.75, 99.82) * mm, "mid": v(62.72, 99.23) * mm, "end": v(61.85, 97.3) * mm});
            skLineSegment(sketch, "E221", {"start": v(61.85, 97.3) * mm, "end": v(61.85, 87.64) * mm});
            skArc(sketch, "E222", {"start": v(42.8, 87.64) * mm, "mid": v(52.32, 78.12) * mm, "end": v(61.85, 87.64) * mm});
            skLineSegment(sketch, "E223", {"start": v(42.8, 87.64) * mm, "end": v(42.8, 99.06) * mm});
            skArc(sketch, "E224", {"start": v(42.8, 99.06) * mm, "mid": v(42.06, 100.86) * mm, "end": v(40.26, 101.6) * mm});
            skLineSegment(sketch, "E225", {"start": v(40.26, 101.6) * mm, "end": v(28.83, 101.6) * mm});
            skArc(sketch, "E226", {"start": v(28.83, 101.6) * mm, "mid": v(27.03, 100.86) * mm, "end": v(26.29, 99.06) * mm});
            skLineSegment(sketch, "E227", {"start": v(26.29, 99.06) * mm, "end": v(26.29, 88.76) * mm});
            skArc(sketch, "E228", {"start": v(7.24, 88.76) * mm, "mid": v(16.76, 79.24) * mm, "end": v(26.29, 88.76) * mm});
            skLineSegment(sketch, "E229", {"start": v(7.24, 88.76) * mm, "end": v(7.24, 99.06) * mm});
            skArc(sketch, "E230", {"start": v(7.24, 99.06) * mm, "mid": v(6.5, 100.86) * mm, "end": v(4.7, 101.6) * mm});
            skLineSegment(sketch, "E231", {"start": v(4.7, 101.6) * mm, "end": v(-6.73, 101.6) * mm});
            skArc(sketch, "E232", {"start": v(-6.73, 101.6) * mm, "mid": v(-8.53, 100.86) * mm, "end": v(-9.27, 99.06) * mm});
            skLineSegment(sketch, "E233", {"start": v(-9.27, 99.06) * mm, "end": v(-9.27, 88.76) * mm});
            skArc(sketch, "E234", {"start": v(-28.32, 88.76) * mm, "mid": v(-18.8, 79.24) * mm, "end": v(-9.27, 88.76) * mm});
            skLineSegment(sketch, "E235", {"start": v(-28.32, 88.76) * mm, "end": v(-28.32, 99.06) * mm});
            skArc(sketch, "E236", {"start": v(-28.32, 99.06) * mm, "mid": v(-29.06, 100.86) * mm, "end": v(-30.86, 101.6) * mm});
            skLineSegment(sketch, "E237", {"start": v(-30.86, 101.6) * mm, "end": v(-42.3, 101.6) * mm});
            skArc(sketch, "E238", {"start": v(-42.3, 101.6) * mm, "mid": v(-44.09, 100.86) * mm, "end": v(-44.83, 99.06) * mm});
            skLineSegment(sketch, "E239", {"start": v(-44.83, 99.06) * mm, "end": v(-44.83, 87.64) * mm});
            skArc(sketch, "E240", {"start": v(-63.88, 87.64) * mm, "mid": v(-54.36, 78.12) * mm, "end": v(-44.83, 87.64) * mm});
            skLineSegment(sketch, "E241", {"start": v(-63.88, 87.64) * mm, "end": v(-63.88, 97.3) * mm});
            skArc(sketch, "E242", {"start": v(-63.88, 97.3) * mm, "mid": v(-64.76, 99.22) * mm, "end": v(-66.78, 99.82) * mm});
            skLineSegment(sketch, "E243", {"start": v(-66.78, 99.82) * mm, "end": v(-78.21, 98.19) * mm});
            skArc(sketch, "E244", {"start": v(-78.21, 98.19) * mm, "mid": v(-79.77, 97.34) * mm, "end": v(-80.4, 95.67) * mm});
            skLineSegment(sketch, "E245", {"start": v(-80.4, 95.67) * mm, "end": v(-80.4, 85.4) * mm});
            skArc(sketch, "E246", {"start": v(-99.44, 85.4) * mm, "mid": v(-89.92, 75.87) * mm, "end": v(-80.4, 85.4) * mm});
            skLineSegment(sketch, "E247", {"start": v(-99.44, 85.4) * mm, "end": v(-99.44, 92.22) * mm});
            skArc(sketch, "E248", {"start": v(-99.44, 92.22) * mm, "mid": v(-100.32, 94.14) * mm, "end": v(-102.34, 94.74) * mm});
            skLineSegment(sketch, "E249", {"start": v(-102.34, 94.74) * mm, "end": v(-113.77, 93.1) * mm});
            skArc(sketch, "E250", {"start": v(-113.77, 93.1) * mm, "mid": v(-115.33, 92.26) * mm, "end": v(-115.95, 90.6) * mm});
            skLineSegment(sketch, "E251", {"start": v(-115.95, 90.6) * mm, "end": v(-115.95, 82.03) * mm});
            skArc(sketch, "E252", {"start": v(-122.27, 73.06) * mm, "mid": v(-117.69, 76.54) * mm, "end": v(-115.95, 82.03) * mm});
            skLineSegment(sketch, "E253", {"start": v(-122.27, 73.06) * mm, "end": v(-141.12, 66.32) * mm});
            skArc(sketch, "E254", {"start": v(-143.97, 65.99) * mm, "mid": v(-142.53, 65.99) * mm, "end": v(-141.12, 66.32) * mm});
            skLineSegment(sketch, "E255", {"start": v(-143.97, 65.99) * mm, "end": v(-162.11, 68.05) * mm});
            skArc(sketch, "E256", {"start": v(-170.56, 77.52) * mm, "mid": v(-168.14, 71.17) * mm, "end": v(-162.11, 68.05) * mm});
            skLineSegment(sketch, "E257", {"start": v(-170.56, 77.52) * mm, "end": v(-170.56, 82.06) * mm});
            skArc(sketch, "E258", {"start": v(-170.56, 82.06) * mm, "mid": v(-171.44, 83.98) * mm, "end": v(-173.46, 84.58) * mm});
            skLineSegment(sketch, "E259", {"start": v(-173.46, 84.58) * mm, "end": v(-184.9, 82.94) * mm});
            skArc(sketch, "E260", {"start": v(-184.9, 82.94) * mm, "mid": v(-186.45, 82.1) * mm, "end": v(-187.07, 80.43) * mm});
            skLineSegment(sketch, "E261", {"start": v(-187.07, 80.43) * mm, "end": v(-187.07, 57.15) * mm});
            skArc(sketch, "E262", {"start": v(-189.61, 54.61) * mm, "mid": v(-187.81, 55.35) * mm, "end": v(-187.07, 57.15) * mm});
            skLineSegment(sketch, "E263", {"start": v(-189.61, 54.61) * mm, "end": v(-209.27, 54.61) * mm});
            skArc(sketch, "E264", {"start": v(-209.27, 54.6) * mm, "mid": v(-211.06, 53.87) * mm, "end": v(-211.8, 52.07) * mm});
            skLineSegment(sketch, "E265", {"start": v(-211.8, 52.07) * mm, "end": v(-211.8, 49.53) * mm});
            skArc(sketch, "E266", {"start": v(-214.35, 47) * mm, "mid": v(-212.55, 47.73) * mm, "end": v(-211.8, 49.53) * mm});
            skLineSegment(sketch, "E267", {"start": v(-214.35, 47) * mm, "end": v(-222.89, 47) * mm});
            skArc(sketch, "E268", {"start": v(-222.89, 47) * mm, "mid": v(-224.68, 46.25) * mm, "end": v(-225.43, 44.45) * mm});
            skLineSegment(sketch, "E269", {"start": v(-47.6, 28.79) * mm, "end": v(47.6, 28.79) * mm});
            skArc(sketch, "E270", {"start": v(-53.95, 35.14) * mm, "mid": v(-52.09, 30.65) * mm, "end": v(-47.6, 28.79) * mm});
            skLineSegment(sketch, "E271", {"start": v(-53.95, 54.19) * mm, "end": v(-53.95, 35.14) * mm});
            skArc(sketch, "E272", {"start": v(-47.6, 60.54) * mm, "mid": v(-52.09, 58.68) * mm, "end": v(-53.95, 54.19) * mm});
            skLineSegment(sketch, "E273", {"start": v(47.6, 60.54) * mm, "end": v(-47.6, 60.54) * mm});
            skArc(sketch, "E274", {"start": v(53.95, 54.19) * mm, "mid": v(52.09, 58.68) * mm, "end": v(47.6, 60.54) * mm});
            skLineSegment(sketch, "E275", {"start": v(53.95, 35.14) * mm, "end": v(53.95, 54.19) * mm});
            skArc(sketch, "E276", {"start": v(47.6, 28.79) * mm, "mid": v(52.09, 30.65) * mm, "end": v(53.95, 35.14) * mm});
            skCircle(sketch, "E277", {"center": v(-73.51, -32.1) * mm, "radius": 1.46 * mm});
            skCircle(sketch, "E278", {"center": v(-193.68, 39.86) * mm, "radius": 1.46 * mm});
            skCircle(sketch, "E279", {"center": v(193.68, 39.86) * mm, "radius": 1.46 * mm});
            skCircle(sketch, "E280", {"center": v(73.51, -32.1) * mm, "radius": 1.46 * mm});
            skSolve(sketch);
        }
        {
            var Q0;
            Q0=qSketchRegion(id+"F2",true);
            extrude(context, id + "F3", {"entities" : qUnion([Q0]), "depth" : 0.01 * mm});
        }
        {
            var Q0;
            Q0=makeQuery(id+"F3.opExtrude","CAP_FACE",FACE,{"disambiguationData":[OSD([sQuery(id+"F2.wireOp",EDGE,"E193"),sQuery(id+"F2.wireOp",EDGE,"E194"),sQuery(id+"F2.wireOp",EDGE,"E195"),sQuery(id+"F2.wireOp",EDGE,"E196"),sQuery(id+"F2.wireOp",EDGE,"E197"),sQuery(id+"F2.wireOp",EDGE,"E198"),sQuery(id+"F2.wireOp",EDGE,"E199"),sQuery(id+"F2.wireOp",EDGE,"E200"),sQuery(id+"F2.wireOp",EDGE,"E201"),sQuery(id+"F2.wireOp",EDGE,"E202"),sQuery(id+"F2.wireOp",EDGE,"E203"),sQuery(id+"F2.wireOp",EDGE,"E204"),sQuery(id+"F2.wireOp",EDGE,"E205"),sQuery(id+"F2.wireOp",EDGE,"E206"),sQuery(id+"F2.wireOp",EDGE,"E207"),sQuery(id+"F2.wireOp",EDGE,"E208"),sQuery(id+"F2.wireOp",EDGE,"E209"),sQuery(id+"F2.wireOp",EDGE,"E210"),sQuery(id+"F2.wireOp",EDGE,"E211"),sQuery(id+"F2.wireOp",EDGE,"E212"),sQuery(id+"F2.wireOp",EDGE,"E213"),sQuery(id+"F2.wireOp",EDGE,"E214"),sQuery(id+"F2.wireOp",EDGE,"E215"),sQuery(id+"F2.wireOp",EDGE,"E216"),sQuery(id+"F2.wireOp",EDGE,"E217"),sQuery(id+"F2.wireOp",EDGE,"E218"),sQuery(id+"F2.wireOp",EDGE,"E219"),sQuery(id+"F2.wireOp",EDGE,"E220"),sQuery(id+"F2.wireOp",EDGE,"E221"),sQuery(id+"F2.wireOp",EDGE,"E222"),sQuery(id+"F2.wireOp",EDGE,"E223"),sQuery(id+"F2.wireOp",EDGE,"E224"),sQuery(id+"F2.wireOp",EDGE,"E225"),sQuery(id+"F2.wireOp",EDGE,"E226"),sQuery(id+"F2.wireOp",EDGE,"E227"),sQuery(id+"F2.wireOp",EDGE,"E228"),sQuery(id+"F2.wireOp",EDGE,"E229"),sQuery(id+"F2.wireOp",EDGE,"E230"),sQuery(id+"F2.wireOp",EDGE,"E231"),sQuery(id+"F2.wireOp",EDGE,"E232"),sQuery(id+"F2.wireOp",EDGE,"E233"),sQuery(id+"F2.wireOp",EDGE,"E234"),sQuery(id+"F2.wireOp",EDGE,"E235"),sQuery(id+"F2.wireOp",EDGE,"E236"),sQuery(id+"F2.wireOp",EDGE,"E237"),sQuery(id+"F2.wireOp",EDGE,"E238"),sQuery(id+"F2.wireOp",EDGE,"E239"),sQuery(id+"F2.wireOp",EDGE,"E240"),sQuery(id+"F2.wireOp",EDGE,"E241"),sQuery(id+"F2.wireOp",EDGE,"E242"),sQuery(id+"F2.wireOp",EDGE,"E243"),sQuery(id+"F2.wireOp",EDGE,"E244"),sQuery(id+"F2.wireOp",EDGE,"E245"),sQuery(id+"F2.wireOp",EDGE,"E246"),sQuery(id+"F2.wireOp",EDGE,"E247"),sQuery(id+"F2.wireOp",EDGE,"E248"),sQuery(id+"F2.wireOp",EDGE,"E249"),sQuery(id+"F2.wireOp",EDGE,"E250"),sQuery(id+"F2.wireOp",EDGE,"E251"),sQuery(id+"F2.wireOp",EDGE,"E252"),sQuery(id+"F2.wireOp",EDGE,"E253"),sQuery(id+"F2.wireOp",EDGE,"E254"),sQuery(id+"F2.wireOp",EDGE,"E255"),sQuery(id+"F2.wireOp",EDGE,"E256"),sQuery(id+"F2.wireOp",EDGE,"E257"),sQuery(id+"F2.wireOp",EDGE,"E258"),sQuery(id+"F2.wireOp",EDGE,"E259"),sQuery(id+"F2.wireOp",EDGE,"E260"),sQuery(id+"F2.wireOp",EDGE,"E261"),sQuery(id+"F2.wireOp",EDGE,"E262"),sQuery(id+"F2.wireOp",EDGE,"E263"),sQuery(id+"F2.wireOp",EDGE,"E264"),sQuery(id+"F2.wireOp",EDGE,"E265"),sQuery(id+"F2.wireOp",EDGE,"E266"),sQuery(id+"F2.wireOp",EDGE,"E267"),sQuery(id+"F2.wireOp",EDGE,"E268"),sQuery(id+"F2.wireOp",EDGE,"E269"),sQuery(id+"F2.wireOp",EDGE,"E270"),sQuery(id+"F2.wireOp",EDGE,"E271"),sQuery(id+"F2.wireOp",EDGE,"E272"),sQuery(id+"F2.wireOp",EDGE,"E273"),sQuery(id+"F2.wireOp",EDGE,"E274"),sQuery(id+"F2.wireOp",EDGE,"E275"),sQuery(id+"F2.wireOp",EDGE,"E276"),sQuery(id+"F2.wireOp",EDGE,"E277"),sQuery(id+"F2.wireOp",EDGE,"E278"),sQuery(id+"F2.wireOp",EDGE,"E279"),sQuery(id+"F2.wireOp",EDGE,"E280")])],"isStart":false});
            var sketch = newSketch(context, id + "F4", { "sketchPlane" : qUnion([Q0])});
            skLineSegment(sketch, "E281", {"start": v(122.27, 73.06) * mm, "end": v(89.92, 75.84) * mm});
            skPoint(sketch, "E281.endSnap0", {"position": v(89.92, 75.87) * mm});
            skLineSegment(sketch, "E282", {"start": v(89.92, 75.84) * mm, "end": v(99.44, 97.3) * mm});
            skLineSegment(sketch, "E283", {"start": v(99.44, 97.3) * mm, "end": v(119.46, 93.1) * mm});
            skLineSegment(sketch, "E284", {"start": v(119.46, 93.1) * mm, "end": v(122.27, 73.06) * mm});
            skSolve(sketch);
        }
        {
            var Q0;
            Q0=qSketchRegion(id+"F4",true);
            var Q1;
            Q1=makeQuery(id+"F1.opExtrude","CAP_FACE",FACE,{"disambiguationData":[OSD([sQuery(id+"F0.wireOp",EDGE,"E0"),sQuery(id+"F0.wireOp",EDGE,"E1"),sQuery(id+"F0.wireOp",EDGE,"E2"),sQuery(id+"F0.wireOp",EDGE,"E3"),sQuery(id+"F0.wireOp",EDGE,"E4"),sQuery(id+"F0.wireOp",EDGE,"E5"),sQuery(id+"F0.wireOp",EDGE,"E6"),sQuery(id+"F0.wireOp",EDGE,"E7"),sQuery(id+"F0.wireOp",EDGE,"E8"),sQuery(id+"F0.wireOp",EDGE,"E9"),sQuery(id+"F0.wireOp",EDGE,"E10"),sQuery(id+"F0.wireOp",EDGE,"E11"),sQuery(id+"F0.wireOp",EDGE,"E12"),sQuery(id+"F0.wireOp",EDGE,"E13"),sQuery(id+"F0.wireOp",EDGE,"E14"),sQuery(id+"F0.wireOp",EDGE,"E15"),sQuery(id+"F0.wireOp",EDGE,"E16"),sQuery(id+"F0.wireOp",EDGE,"E17"),sQuery(id+"F0.wireOp",EDGE,"E18"),sQuery(id+"F0.wireOp",EDGE,"E19"),sQuery(id+"F0.wireOp",EDGE,"E20"),sQuery(id+"F0.wireOp",EDGE,"E21"),sQuery(id+"F0.wireOp",EDGE,"E22"),sQuery(id+"F0.wireOp",EDGE,"E23"),sQuery(id+"F0.wireOp",EDGE,"E24"),sQuery(id+"F0.wireOp",EDGE,"E25"),sQuery(id+"F0.wireOp",EDGE,"E26"),sQuery(id+"F0.wireOp",EDGE,"E27"),sQuery(id+"F0.wireOp",EDGE,"E28"),sQuery(id+"F0.wireOp",EDGE,"E29"),sQuery(id+"F0.wireOp",EDGE,"E30"),sQuery(id+"F0.wireOp",EDGE,"E31"),sQuery(id+"F0.wireOp",EDGE,"E32"),sQuery(id+"F0.wireOp",EDGE,"E33"),sQuery(id+"F0.wireOp",EDGE,"E34"),sQuery(id+"F0.wireOp",EDGE,"E35"),sQuery(id+"F0.wireOp",EDGE,"E36"),sQuery(id+"F0.wireOp",EDGE,"E37"),sQuery(id+"F0.wireOp",EDGE,"E38"),sQuery(id+"F0.wireOp",EDGE,"E39"),sQuery(id+"F0.wireOp",EDGE,"E40"),sQuery(id+"F0.wireOp",EDGE,"E41"),sQuery(id+"F0.wireOp",EDGE,"E42"),sQuery(id+"F0.wireOp",EDGE,"E43"),sQuery(id+"F0.wireOp",EDGE,"E44"),sQuery(id+"F0.wireOp",EDGE,"E45"),sQuery(id+"F0.wireOp",EDGE,"E46"),sQuery(id+"F0.wireOp",EDGE,"E47"),sQuery(id+"F0.wireOp",EDGE,"E48"),sQuery(id+"F0.wireOp",EDGE,"E49"),sQuery(id+"F0.wireOp",EDGE,"E50"),sQuery(id+"F0.wireOp",EDGE,"E51"),sQuery(id+"F0.wireOp",EDGE,"E52"),sQuery(id+"F0.wireOp",EDGE,"E53"),sQuery(id+"F0.wireOp",EDGE,"E54"),sQuery(id+"F0.wireOp",EDGE,"E55"),sQuery(id+"F0.wireOp",EDGE,"E56"),sQuery(id+"F0.wireOp",EDGE,"E57"),sQuery(id+"F0.wireOp",EDGE,"E58"),sQuery(id+"F0.wireOp",EDGE,"E59"),sQuery(id+"F0.wireOp",EDGE,"E60"),sQuery(id+"F0.wireOp",EDGE,"E61"),sQuery(id+"F0.wireOp",EDGE,"E62"),sQuery(id+"F0.wireOp",EDGE,"E63"),sQuery(id+"F0.wireOp",EDGE,"E64"),sQuery(id+"F0.wireOp",EDGE,"E65"),sQuery(id+"F0.wireOp",EDGE,"E66"),sQuery(id+"F0.wireOp",EDGE,"E67"),sQuery(id+"F0.wireOp",EDGE,"E68"),sQuery(id+"F0.wireOp",EDGE,"E69"),sQuery(id+"F0.wireOp",EDGE,"E70"),sQuery(id+"F0.wireOp",EDGE,"E71"),sQuery(id+"F0.wireOp",EDGE,"E72"),sQuery(id+"F0.wireOp",EDGE,"E73"),sQuery(id+"F0.wireOp",EDGE,"E74"),sQuery(id+"F0.wireOp",EDGE,"E75"),sQuery(id+"F0.wireOp",EDGE,"E76"),sQuery(id+"F0.wireOp",EDGE,"E77"),sQuery(id+"F0.wireOp",EDGE,"E78"),sQuery(id+"F0.wireOp",EDGE,"E79"),sQuery(id+"F0.wireOp",EDGE,"E80"),sQuery(id+"F0.wireOp",EDGE,"E81"),sQuery(id+"F0.wireOp",EDGE,"E82"),sQuery(id+"F0.wireOp",EDGE,"E83"),sQuery(id+"F0.wireOp",EDGE,"E84"),sQuery(id+"F0.wireOp",EDGE,"E85"),sQuery(id+"F0.wireOp",EDGE,"E86"),sQuery(id+"F0.wireOp",EDGE,"E87"),sQuery(id+"F0.wireOp",EDGE,"E88"),sQuery(id+"F0.wireOp",EDGE,"E89"),sQuery(id+"F0.wireOp",EDGE,"E90"),sQuery(id+"F0.wireOp",EDGE,"E91"),sQuery(id+"F0.wireOp",EDGE,"E92"),sQuery(id+"F0.wireOp",EDGE,"E93"),sQuery(id+"F0.wireOp",EDGE,"E94"),sQuery(id+"F0.wireOp",EDGE,"E95"),sQuery(id+"F0.wireOp",EDGE,"E96"),sQuery(id+"F0.wireOp",EDGE,"E97"),sQuery(id+"F0.wireOp",EDGE,"E98"),sQuery(id+"F0.wireOp",EDGE,"E99"),sQuery(id+"F0.wireOp",EDGE,"E100"),sQuery(id+"F0.wireOp",EDGE,"E101"),sQuery(id+"F0.wireOp",EDGE,"E102"),sQuery(id+"F0.wireOp",EDGE,"E103"),sQuery(id+"F0.wireOp",EDGE,"E104"),sQuery(id+"F0.wireOp",EDGE,"E105"),sQuery(id+"F0.wireOp",EDGE,"E106"),sQuery(id+"F0.wireOp",EDGE,"E107"),sQuery(id+"F0.wireOp",EDGE,"E108"),sQuery(id+"F0.wireOp",EDGE,"E109"),sQuery(id+"F0.wireOp",EDGE,"E110"),sQuery(id+"F0.wireOp",EDGE,"E111"),sQuery(id+"F0.wireOp",EDGE,"E112"),sQuery(id+"F0.wireOp",EDGE,"E113"),sQuery(id+"F0.wireOp",EDGE,"E114"),sQuery(id+"F0.wireOp",EDGE,"E115"),sQuery(id+"F0.wireOp",EDGE,"E116"),sQuery(id+"F0.wireOp",EDGE,"E117"),sQuery(id+"F0.wireOp",EDGE,"E118"),sQuery(id+"F0.wireOp",EDGE,"E119"),sQuery(id+"F0.wireOp",EDGE,"E120"),sQuery(id+"F0.wireOp",EDGE,"E121"),sQuery(id+"F0.wireOp",EDGE,"E122"),sQuery(id+"F0.wireOp",EDGE,"E123"),sQuery(id+"F0.wireOp",EDGE,"E124"),sQuery(id+"F0.wireOp",EDGE,"E125"),sQuery(id+"F0.wireOp",EDGE,"E126"),sQuery(id+"F0.wireOp",EDGE,"E127"),sQuery(id+"F0.wireOp",EDGE,"E128"),sQuery(id+"F0.wireOp",EDGE,"E129"),sQuery(id+"F0.wireOp",EDGE,"E130"),sQuery(id+"F0.wireOp",EDGE,"E131"),sQuery(id+"F0.wireOp",EDGE,"E132"),sQuery(id+"F0.wireOp",EDGE,"E133"),sQuery(id+"F0.wireOp",EDGE,"E134"),sQuery(id+"F0.wireOp",EDGE,"E135"),sQuery(id+"F0.wireOp",EDGE,"E136"),sQuery(id+"F0.wireOp",EDGE,"E137"),sQuery(id+"F0.wireOp",EDGE,"E138"),sQuery(id+"F0.wireOp",EDGE,"E139"),sQuery(id+"F0.wireOp",EDGE,"E140"),sQuery(id+"F0.wireOp",EDGE,"E141"),sQuery(id+"F0.wireOp",EDGE,"E142"),sQuery(id+"F0.wireOp",EDGE,"E143"),sQuery(id+"F0.wireOp",EDGE,"E144"),sQuery(id+"F0.wireOp",EDGE,"E145"),sQuery(id+"F0.wireOp",EDGE,"E146"),sQuery(id+"F0.wireOp",EDGE,"E147"),sQuery(id+"F0.wireOp",EDGE,"E148"),sQuery(id+"F0.wireOp",EDGE,"E149"),sQuery(id+"F0.wireOp",EDGE,"E150"),sQuery(id+"F0.wireOp",EDGE,"E151"),sQuery(id+"F0.wireOp",EDGE,"E152"),sQuery(id+"F0.wireOp",EDGE,"E153"),sQuery(id+"F0.wireOp",EDGE,"E154"),sQuery(id+"F0.wireOp",EDGE,"E155"),sQuery(id+"F0.wireOp",EDGE,"E156"),sQuery(id+"F0.wireOp",EDGE,"E157"),sQuery(id+"F0.wireOp",EDGE,"E158"),sQuery(id+"F0.wireOp",EDGE,"E159"),sQuery(id+"F0.wireOp",EDGE,"E160"),sQuery(id+"F0.wireOp",EDGE,"E161"),sQuery(id+"F0.wireOp",EDGE,"E162"),sQuery(id+"F0.wireOp",EDGE,"E163"),sQuery(id+"F0.wireOp",EDGE,"E164"),sQuery(id+"F0.wireOp",EDGE,"E165"),sQuery(id+"F0.wireOp",EDGE,"E166"),sQuery(id+"F0.wireOp",EDGE,"E167"),sQuery(id+"F0.wireOp",EDGE,"E168"),sQuery(id+"F0.wireOp",EDGE,"E169"),sQuery(id+"F0.wireOp",EDGE,"E170"),sQuery(id+"F0.wireOp",EDGE,"E171"),sQuery(id+"F0.wireOp",EDGE,"E172"),sQuery(id+"F0.wireOp",EDGE,"E173"),sQuery(id+"F0.wireOp",EDGE,"E174"),sQuery(id+"F0.wireOp",EDGE,"E175"),sQuery(id+"F0.wireOp",EDGE,"E176"),sQuery(id+"F0.wireOp",EDGE,"E177"),sQuery(id+"F0.wireOp",EDGE,"E178"),sQuery(id+"F0.wireOp",EDGE,"E179"),sQuery(id+"F0.wireOp",EDGE,"E180"),sQuery(id+"F0.wireOp",EDGE,"E181"),sQuery(id+"F0.wireOp",EDGE,"E182"),sQuery(id+"F0.wireOp",EDGE,"E183"),sQuery(id+"F0.wireOp",EDGE,"E184"),sQuery(id+"F0.wireOp",EDGE,"E185"),sQuery(id+"F0.wireOp",EDGE,"E186"),sQuery(id+"F0.wireOp",EDGE,"E187"),sQuery(id+"F0.wireOp",EDGE,"E188"),sQuery(id+"F0.wireOp",EDGE,"E189"),sQuery(id+"F0.wireOp",EDGE,"E190"),sQuery(id+"F0.wireOp",EDGE,"E191"),sQuery(id+"F0.wireOp",EDGE,"E192")])],"isStart":true});
            extrude(context, id + "F5", {"entities" : qUnion([Q0]), "operationType" : NewBodyOperationType.REMOVE, "endBound" : BoundingType.UP_TO_SURFACE, "oppositeDirection" : true, "endBoundEntityFace" : qUnion([Q1]), "depth" : 70.87 * mm});
        }
        {
            var Q0;
            Q0=makeQuery(id+"F5.boolean.opBoolean","SPLIT",BODY,{"disambiguationData":[OD(0.0)],"derivedFrom":makeQuery(id+"F3.opExtrude","SWEPT_BODY",BODY,{"disambiguationData":[OSD([sQuery(id+"F2.wireOp",EDGE,"E193"),sQuery(id+"F2.wireOp",EDGE,"E194"),sQuery(id+"F2.wireOp",EDGE,"E195"),sQuery(id+"F2.wireOp",EDGE,"E196"),sQuery(id+"F2.wireOp",EDGE,"E197"),sQuery(id+"F2.wireOp",EDGE,"E198"),sQuery(id+"F2.wireOp",EDGE,"E199"),sQuery(id+"F2.wireOp",EDGE,"E200"),sQuery(id+"F2.wireOp",EDGE,"E201"),sQuery(id+"F2.wireOp",EDGE,"E202"),sQuery(id+"F2.wireOp",EDGE,"E203"),sQuery(id+"F2.wireOp",EDGE,"E204"),sQuery(id+"F2.wireOp",EDGE,"E205"),sQuery(id+"F2.wireOp",EDGE,"E206"),sQuery(id+"F2.wireOp",EDGE,"E207"),sQuery(id+"F2.wireOp",EDGE,"E208"),sQuery(id+"F2.wireOp",EDGE,"E209"),sQuery(id+"F2.wireOp",EDGE,"E210"),sQuery(id+"F2.wireOp",EDGE,"E211"),sQuery(id+"F2.wireOp",EDGE,"E212"),sQuery(id+"F2.wireOp",EDGE,"E213"),sQuery(id+"F2.wireOp",EDGE,"E214"),sQuery(id+"F2.wireOp",EDGE,"E215"),sQuery(id+"F2.wireOp",EDGE,"E216"),sQuery(id+"F2.wireOp",EDGE,"E217"),sQuery(id+"F2.wireOp",EDGE,"E218"),sQuery(id+"F2.wireOp",EDGE,"E219"),sQuery(id+"F2.wireOp",EDGE,"E220"),sQuery(id+"F2.wireOp",EDGE,"E221"),sQuery(id+"F2.wireOp",EDGE,"E222"),sQuery(id+"F2.wireOp",EDGE,"E223"),sQuery(id+"F2.wireOp",EDGE,"E224"),sQuery(id+"F2.wireOp",EDGE,"E225"),sQuery(id+"F2.wireOp",EDGE,"E226"),sQuery(id+"F2.wireOp",EDGE,"E227"),sQuery(id+"F2.wireOp",EDGE,"E228"),sQuery(id+"F2.wireOp",EDGE,"E229"),sQuery(id+"F2.wireOp",EDGE,"E230"),sQuery(id+"F2.wireOp",EDGE,"E231"),sQuery(id+"F2.wireOp",EDGE,"E232"),sQuery(id+"F2.wireOp",EDGE,"E233"),sQuery(id+"F2.wireOp",EDGE,"E234"),sQuery(id+"F2.wireOp",EDGE,"E235"),sQuery(id+"F2.wireOp",EDGE,"E236"),sQuery(id+"F2.wireOp",EDGE,"E237"),sQuery(id+"F2.wireOp",EDGE,"E238"),sQuery(id+"F2.wireOp",EDGE,"E239"),sQuery(id+"F2.wireOp",EDGE,"E240"),sQuery(id+"F2.wireOp",EDGE,"E241"),sQuery(id+"F2.wireOp",EDGE,"E242"),sQuery(id+"F2.wireOp",EDGE,"E243"),sQuery(id+"F2.wireOp",EDGE,"E244"),sQuery(id+"F2.wireOp",EDGE,"E245"),sQuery(id+"F2.wireOp",EDGE,"E246"),sQuery(id+"F2.wireOp",EDGE,"E247"),sQuery(id+"F2.wireOp",EDGE,"E248"),sQuery(id+"F2.wireOp",EDGE,"E249"),sQuery(id+"F2.wireOp",EDGE,"E250"),sQuery(id+"F2.wireOp",EDGE,"E251"),sQuery(id+"F2.wireOp",EDGE,"E252"),sQuery(id+"F2.wireOp",EDGE,"E253"),sQuery(id+"F2.wireOp",EDGE,"E254"),sQuery(id+"F2.wireOp",EDGE,"E255"),sQuery(id+"F2.wireOp",EDGE,"E256"),sQuery(id+"F2.wireOp",EDGE,"E257"),sQuery(id+"F2.wireOp",EDGE,"E258"),sQuery(id+"F2.wireOp",EDGE,"E259"),sQuery(id+"F2.wireOp",EDGE,"E260"),sQuery(id+"F2.wireOp",EDGE,"E261"),sQuery(id+"F2.wireOp",EDGE,"E262"),sQuery(id+"F2.wireOp",EDGE,"E263"),sQuery(id+"F2.wireOp",EDGE,"E264"),sQuery(id+"F2.wireOp",EDGE,"E265"),sQuery(id+"F2.wireOp",EDGE,"E266"),sQuery(id+"F2.wireOp",EDGE,"E267"),sQuery(id+"F2.wireOp",EDGE,"E268"),sQuery(id+"F2.wireOp",EDGE,"E269"),sQuery(id+"F2.wireOp",EDGE,"E270"),sQuery(id+"F2.wireOp",EDGE,"E271"),sQuery(id+"F2.wireOp",EDGE,"E272"),sQuery(id+"F2.wireOp",EDGE,"E273"),sQuery(id+"F2.wireOp",EDGE,"E274"),sQuery(id+"F2.wireOp",EDGE,"E275"),sQuery(id+"F2.wireOp",EDGE,"E276"),sQuery(id+"F2.wireOp",EDGE,"E277"),sQuery(id+"F2.wireOp",EDGE,"E278"),sQuery(id+"F2.wireOp",EDGE,"E279"),sQuery(id+"F2.wireOp",EDGE,"E280")])]})});
            var Q1;
            Q1=makeQuery(id+"F3.opExtrude","CAP_EDGE",EDGE,{"disambiguationData":[OSD([sQuery(id+"F2.wireOp",EDGE,"E269")])],"isStart":false});
            var Q2;
            Q2=makeQuery(id+"F1.opExtrude","CAP_EDGE",EDGE,{"disambiguationData":[OSD([sQuery(id+"F0.wireOp",EDGE,"E161")])],"isStart":true});
            transform(context, id + "F6", {"entities" : qUnion([Q0]), "transformType" : TransformType.TRANSLATION_DISTANCE, "transformDirection" : qUnion([Q2]), "distance" : 52.83 * mm, "makeCopy" : false});
        }
        {
            var Q0;
            Q0=makeQuery(id+"F5.boolean.opBoolean","SPLIT",BODY,{"disambiguationData":[OD(0.0)],"derivedFrom":makeQuery(id+"F3.opExtrude","SWEPT_BODY",BODY,{"disambiguationData":[OSD([sQuery(id+"F2.wireOp",EDGE,"E193"),sQuery(id+"F2.wireOp",EDGE,"E194"),sQuery(id+"F2.wireOp",EDGE,"E195"),sQuery(id+"F2.wireOp",EDGE,"E196"),sQuery(id+"F2.wireOp",EDGE,"E197"),sQuery(id+"F2.wireOp",EDGE,"E198"),sQuery(id+"F2.wireOp",EDGE,"E199"),sQuery(id+"F2.wireOp",EDGE,"E200"),sQuery(id+"F2.wireOp",EDGE,"E201"),sQuery(id+"F2.wireOp",EDGE,"E202"),sQuery(id+"F2.wireOp",EDGE,"E203"),sQuery(id+"F2.wireOp",EDGE,"E204"),sQuery(id+"F2.wireOp",EDGE,"E205"),sQuery(id+"F2.wireOp",EDGE,"E206"),sQuery(id+"F2.wireOp",EDGE,"E207"),sQuery(id+"F2.wireOp",EDGE,"E208"),sQuery(id+"F2.wireOp",EDGE,"E209"),sQuery(id+"F2.wireOp",EDGE,"E210"),sQuery(id+"F2.wireOp",EDGE,"E211"),sQuery(id+"F2.wireOp",EDGE,"E212"),sQuery(id+"F2.wireOp",EDGE,"E213"),sQuery(id+"F2.wireOp",EDGE,"E214"),sQuery(id+"F2.wireOp",EDGE,"E215"),sQuery(id+"F2.wireOp",EDGE,"E216"),sQuery(id+"F2.wireOp",EDGE,"E217"),sQuery(id+"F2.wireOp",EDGE,"E218"),sQuery(id+"F2.wireOp",EDGE,"E219"),sQuery(id+"F2.wireOp",EDGE,"E220"),sQuery(id+"F2.wireOp",EDGE,"E221"),sQuery(id+"F2.wireOp",EDGE,"E222"),sQuery(id+"F2.wireOp",EDGE,"E223"),sQuery(id+"F2.wireOp",EDGE,"E224"),sQuery(id+"F2.wireOp",EDGE,"E225"),sQuery(id+"F2.wireOp",EDGE,"E226"),sQuery(id+"F2.wireOp",EDGE,"E227"),sQuery(id+"F2.wireOp",EDGE,"E228"),sQuery(id+"F2.wireOp",EDGE,"E229"),sQuery(id+"F2.wireOp",EDGE,"E230"),sQuery(id+"F2.wireOp",EDGE,"E231"),sQuery(id+"F2.wireOp",EDGE,"E232"),sQuery(id+"F2.wireOp",EDGE,"E233"),sQuery(id+"F2.wireOp",EDGE,"E234"),sQuery(id+"F2.wireOp",EDGE,"E235"),sQuery(id+"F2.wireOp",EDGE,"E236"),sQuery(id+"F2.wireOp",EDGE,"E237"),sQuery(id+"F2.wireOp",EDGE,"E238"),sQuery(id+"F2.wireOp",EDGE,"E239"),sQuery(id+"F2.wireOp",EDGE,"E240"),sQuery(id+"F2.wireOp",EDGE,"E241"),sQuery(id+"F2.wireOp",EDGE,"E242"),sQuery(id+"F2.wireOp",EDGE,"E243"),sQuery(id+"F2.wireOp",EDGE,"E244"),sQuery(id+"F2.wireOp",EDGE,"E245"),sQuery(id+"F2.wireOp",EDGE,"E246"),sQuery(id+"F2.wireOp",EDGE,"E247"),sQuery(id+"F2.wireOp",EDGE,"E248"),sQuery(id+"F2.wireOp",EDGE,"E249"),sQuery(id+"F2.wireOp",EDGE,"E250"),sQuery(id+"F2.wireOp",EDGE,"E251"),sQuery(id+"F2.wireOp",EDGE,"E252"),sQuery(id+"F2.wireOp",EDGE,"E253"),sQuery(id+"F2.wireOp",EDGE,"E254"),sQuery(id+"F2.wireOp",EDGE,"E255"),sQuery(id+"F2.wireOp",EDGE,"E256"),sQuery(id+"F2.wireOp",EDGE,"E257"),sQuery(id+"F2.wireOp",EDGE,"E258"),sQuery(id+"F2.wireOp",EDGE,"E259"),sQuery(id+"F2.wireOp",EDGE,"E260"),sQuery(id+"F2.wireOp",EDGE,"E261"),sQuery(id+"F2.wireOp",EDGE,"E262"),sQuery(id+"F2.wireOp",EDGE,"E263"),sQuery(id+"F2.wireOp",EDGE,"E264"),sQuery(id+"F2.wireOp",EDGE,"E265"),sQuery(id+"F2.wireOp",EDGE,"E266"),sQuery(id+"F2.wireOp",EDGE,"E267"),sQuery(id+"F2.wireOp",EDGE,"E268"),sQuery(id+"F2.wireOp",EDGE,"E269"),sQuery(id+"F2.wireOp",EDGE,"E270"),sQuery(id+"F2.wireOp",EDGE,"E271"),sQuery(id+"F2.wireOp",EDGE,"E272"),sQuery(id+"F2.wireOp",EDGE,"E273"),sQuery(id+"F2.wireOp",EDGE,"E274"),sQuery(id+"F2.wireOp",EDGE,"E275"),sQuery(id+"F2.wireOp",EDGE,"E276"),sQuery(id+"F2.wireOp",EDGE,"E277"),sQuery(id+"F2.wireOp",EDGE,"E278"),sQuery(id+"F2.wireOp",EDGE,"E279"),sQuery(id+"F2.wireOp",EDGE,"E280")])]})});
            var Q1;
            Q1=makeQuery(id+"F1.opExtrude","CAP_EDGE",EDGE,{"disambiguationData":[OSD([sQuery(id+"F0.wireOp",EDGE,"E168")])],"isStart":true});
            transform(context, id + "F7", {"entities" : qUnion([Q0]), "transformType" : TransformType.TRANSLATION_DISTANCE, "transformDirection" : qUnion([Q1]), "distance" : 37.34 * mm, "oppositeDirection" : true, "makeCopy" : false});
        }
    });
